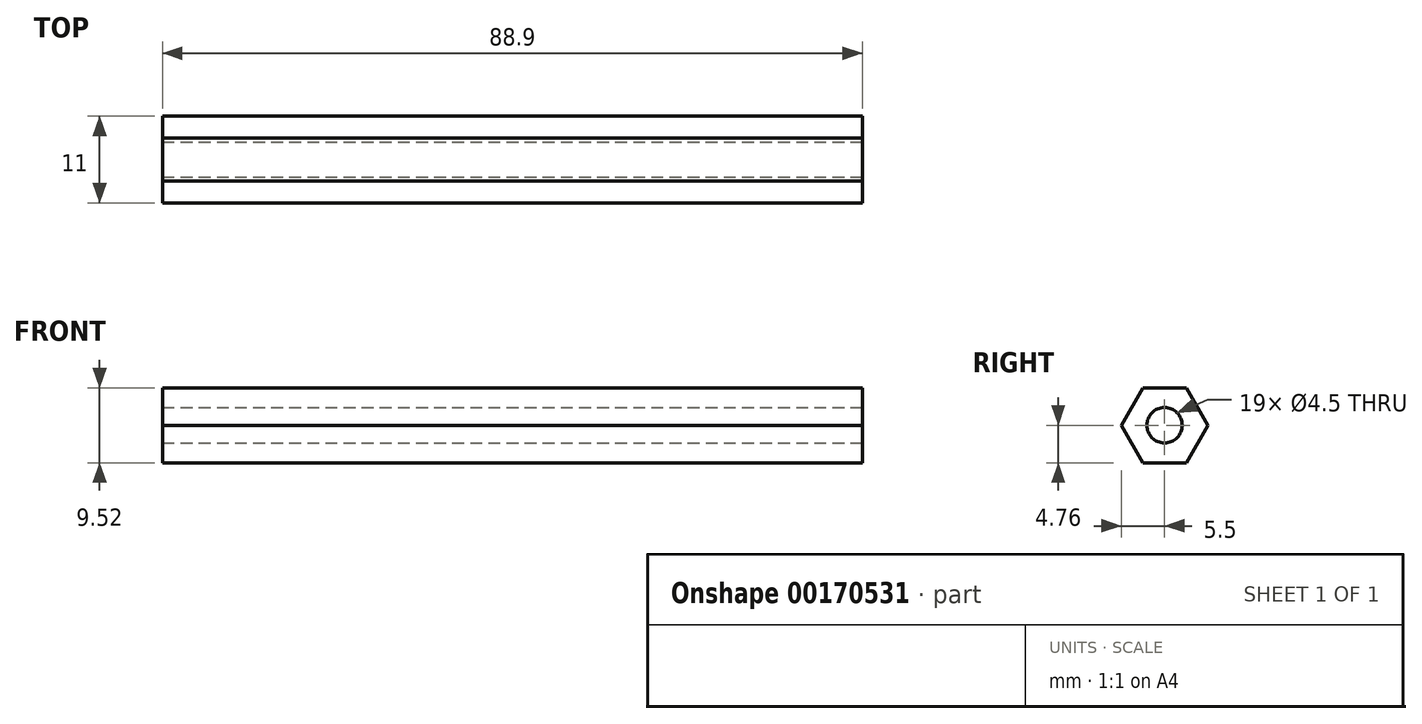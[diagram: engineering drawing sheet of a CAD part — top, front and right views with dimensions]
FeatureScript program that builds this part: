
annotation { "Feature Type Name" : "Feature", "Feature Type Description" : "" }
export const myFeature = defineFeature(function(context is Context, id is Id, definition is map)
    precondition{}
    {
        {
            var Q0;
            Q0=qCreatedBy(makeId("Right.planeOp"),FACE);
            var sketch = newSketch(context, id + "F0", { "sketchPlane" : qUnion([Q0])});
            skCircle(sketch, "E0.cCircle", {"center": v(0, 0) * mm, "radius": 4.76 * mm, "construction": true});
            skLineSegment(sketch, "E0.0", {"start": v(2.75, 4.76) * mm, "end": v(5.5, 0) * mm});
            skLineSegment(sketch, "E0.1", {"start": v(5.5, 0) * mm, "end": v(2.75, -4.76) * mm});
            skLineSegment(sketch, "E0.2", {"start": v(2.75, -4.76) * mm, "end": v(-2.75, -4.76) * mm});
            skLineSegment(sketch, "E0.3", {"start": v(-2.75, -4.76) * mm, "end": v(-5.5, 0) * mm});
            skLineSegment(sketch, "E0.4", {"start": v(-5.5, 0) * mm, "end": v(-2.75, 4.76) * mm});
            skLineSegment(sketch, "E0.5", {"start": v(-2.75, 4.76) * mm, "end": v(2.75, 4.76) * mm});
            skPoint(sketch, "E0.0.midPoint", {"position": v(4.12, 2.38) * mm});
            skSolve(sketch);
        }
        {
            var Q0;
            Q0=makeQuery(id+"F0.imprint","IMPRINT",FACE,{"disambiguationData":[TD([[makeQuery(id+"F0.imprint","IMPRINT",EDGE,{"derivedFrom":sQuery(id+"F0.wireOp",EDGE,"E0.0")}),-1.0]])]});
            extrude(context, id + "F1", {"entities" : qUnion([Q0]), "oppositeDirection" : true, "depth" : 88.9 * mm});
        }
        {
            var Q0;
            Q0=makeQuery(id+"F1.opExtrude","CAP_FACE",FACE,{"disambiguationData":[OSD([sQuery(id+"F0.wireOp",EDGE,"E0.0"),sQuery(id+"F0.wireOp",EDGE,"E0.1"),sQuery(id+"F0.wireOp",EDGE,"E0.2"),sQuery(id+"F0.wireOp",EDGE,"E0.3"),sQuery(id+"F0.wireOp",EDGE,"E0.4"),sQuery(id+"F0.wireOp",EDGE,"E0.5")])],"isStart":true});
            var sketch = newSketch(context, id + "F2", { "sketchPlane" : qUnion([Q0])});
            skCircle(sketch, "E1", {"center": v(0, 0) * mm, "radius": 2.55 * mm, "construction": true});
            skSolve(sketch);
        }
        {
            var Q0;
            Q0=sQuery(id+"F2.wireOp",VERTEX,"E1.center");
            var Q1;
            Q1=makeQuery(id+"F1.opExtrude","SWEPT_BODY",BODY,{"disambiguationData":[OSD([sQuery(id+"F0.wireOp",EDGE,"E0.0"),sQuery(id+"F0.wireOp",EDGE,"E0.1"),sQuery(id+"F0.wireOp",EDGE,"E0.2"),sQuery(id+"F0.wireOp",EDGE,"E0.3"),sQuery(id+"F0.wireOp",EDGE,"E0.4"),sQuery(id+"F0.wireOp",EDGE,"E0.5")])]});
            hole(context, id + "F3", {"style" : HoleStyle.SIMPLE, "endStyle" : HoleEndStyle.THROUGH, "holeDiameter" : 4.5 * mm, "locations" : qUnion([Q0]), "scope" : qUnion([Q1]), "isTappedThrough" : true});
        }
    });
